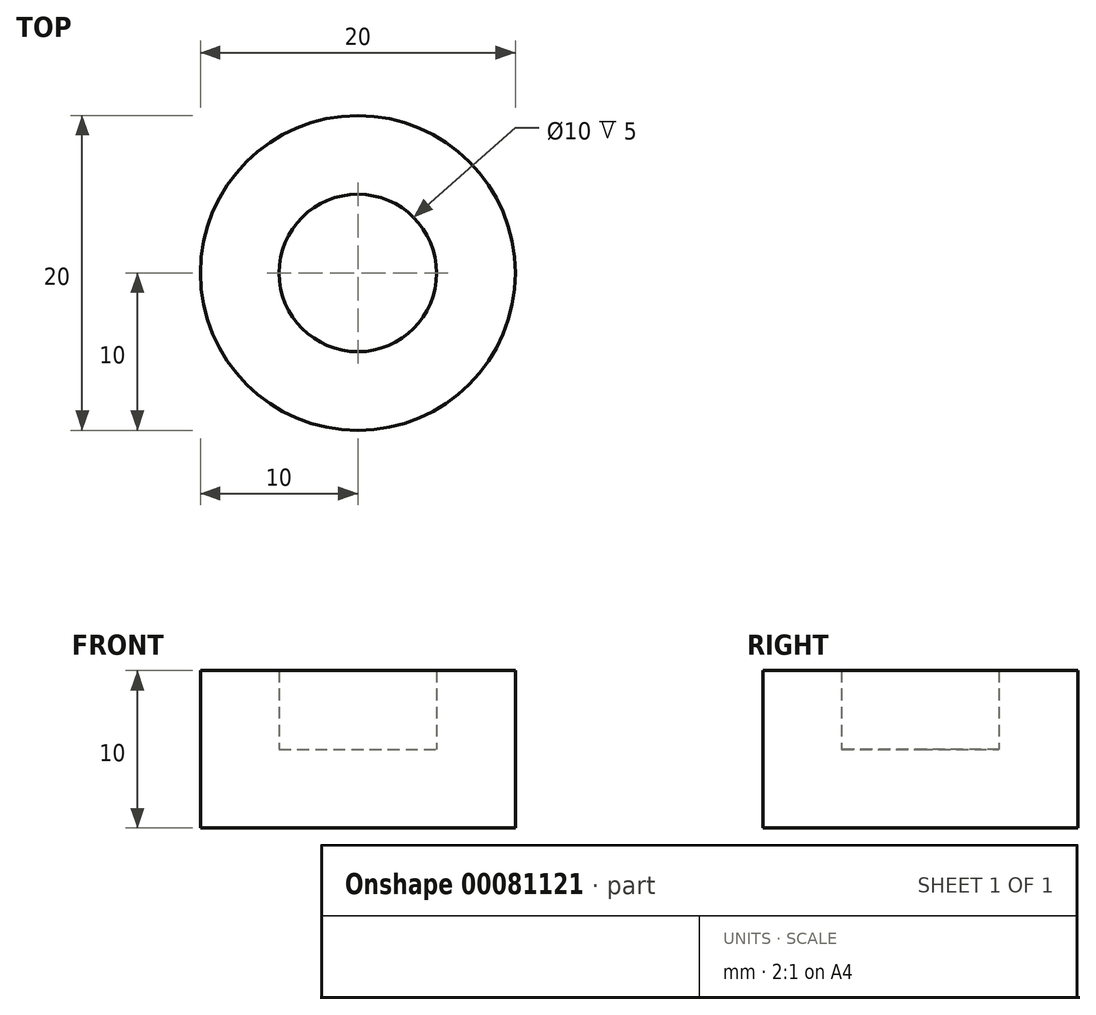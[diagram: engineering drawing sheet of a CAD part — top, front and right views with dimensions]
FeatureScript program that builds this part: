
annotation { "Feature Type Name" : "Feature", "Feature Type Description" : "" }
export const myFeature = defineFeature(function(context is Context, id is Id, definition is map)
    precondition{}
    {
        {
            var Q0;
            Q0=qCreatedBy(makeId("Front.planeOp"),FACE);
            var sketch = newSketch(context, id + "F0", { "sketchPlane" : qUnion([Q0])});
            skLineSegment(sketch, "E0", {"start": v(0, 0) * mm, "end": v(0, 5) * mm});
            skLineSegment(sketch, "E1", {"start": v(0, 5) * mm, "end": v(5, 5) * mm});
            skLineSegment(sketch, "E2", {"start": v(5, 5) * mm, "end": v(5, 10) * mm});
            skLineSegment(sketch, "E3", {"start": v(5, 10) * mm, "end": v(10, 10) * mm});
            skLineSegment(sketch, "E4", {"start": v(10, 10) * mm, "end": v(10, 0) * mm});
            skLineSegment(sketch, "E5", {"start": v(10, 0) * mm, "end": v(0, 0) * mm});
            skSolve(sketch);
        }
        {
            var Q0;
            Q0=makeQuery(id+"F0.imprint","IMPRINT",FACE,{"disambiguationData":[TD([[makeQuery(id+"F0.imprint","IMPRINT",EDGE,{"derivedFrom":sQuery(id+"F0.wireOp",EDGE,"E0")}),-1.0]])]});
            var Q1;
            Q1=sQuery(id+"F0.wireOp",EDGE,"E0");
            revolve(context, id + "F1", {"entities" : qUnion([Q0]), "axis" : qUnion([Q1]), "revolveType" : RevolveType.FULL});
        }
    });
